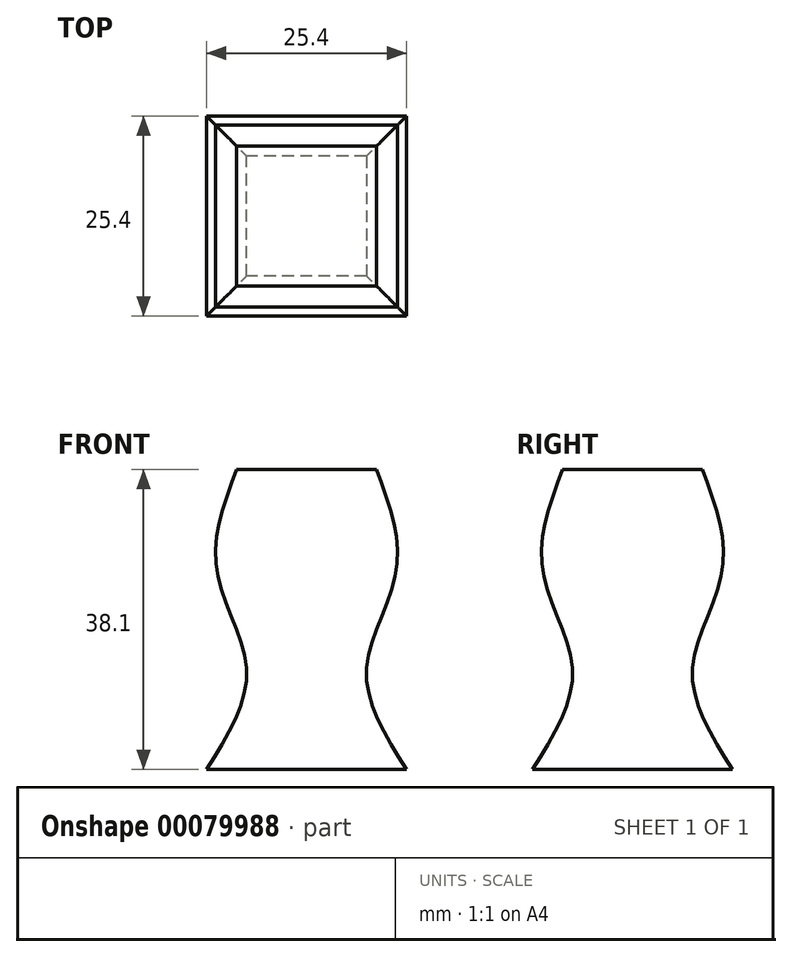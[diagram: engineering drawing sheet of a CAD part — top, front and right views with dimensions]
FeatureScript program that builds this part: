
annotation { "Feature Type Name" : "Feature", "Feature Type Description" : "" }
export const myFeature = defineFeature(function(context is Context, id is Id, definition is map)
    precondition{}
    {
        {
            var Q0;
            Q0=qCreatedBy(makeId("Top.planeOp"),FACE);
            cPlane(context, id + "F0", {"entities" : qUnion([Q0]), "cplaneType" : CPlaneType.OFFSET, "offset" : 12.7 * mm, "width" : 152.4 * mm, "height" : 152.4 * mm});
        }
        {
            var Q0;
            Q0=qCreatedBy(id+"F0.planeOp",FACE);
            cPlane(context, id + "F1", {"entities" : qUnion([Q0]), "cplaneType" : CPlaneType.OFFSET, "offset" : 12.7 * mm, "width" : 152.4 * mm, "height" : 152.4 * mm});
        }
        {
            var Q0;
            Q0=qCreatedBy(id+"F1.planeOp",FACE);
            cPlane(context, id + "F2", {"entities" : qUnion([Q0]), "cplaneType" : CPlaneType.OFFSET, "offset" : 12.7 * mm, "width" : 152.4 * mm, "height" : 152.4 * mm});
        }
        {
            var Q0;
            Q0=qCreatedBy(makeId("Top.planeOp"),FACE);
            var sketch = newSketch(context, id + "F3", { "sketchPlane" : qUnion([Q0])});
            skLineSegment(sketch, "E0.bottom", {"start": v(-12.7, 12.7) * mm, "end": v(12.7, 12.7) * mm});
            skLineSegment(sketch, "E0.top", {"start": v(-12.7, -12.7) * mm, "end": v(12.7, -12.7) * mm});
            skLineSegment(sketch, "E0.left", {"start": v(-12.7, 12.7) * mm, "end": v(-12.7, -12.7) * mm});
            skLineSegment(sketch, "E0.right", {"start": v(12.7, 12.7) * mm, "end": v(12.7, -12.7) * mm});
            skSolve(sketch);
        }
        {
            var Q0;
            Q0=qCreatedBy(id+"F0.planeOp",FACE);
            var sketch = newSketch(context, id + "F4", { "sketchPlane" : qUnion([Q0])});
            skLineSegment(sketch, "E1.bottom", {"start": v(-7.62, 7.62) * mm, "end": v(7.62, 7.62) * mm});
            skLineSegment(sketch, "E1.top", {"start": v(-7.62, -7.62) * mm, "end": v(7.62, -7.62) * mm});
            skLineSegment(sketch, "E1.left", {"start": v(-7.62, 7.62) * mm, "end": v(-7.62, -7.62) * mm});
            skLineSegment(sketch, "E1.right", {"start": v(7.62, 7.62) * mm, "end": v(7.62, -7.62) * mm});
            skSolve(sketch);
        }
        {
            var Q0;
            Q0=qCreatedBy(id+"F1.planeOp",FACE);
            var sketch = newSketch(context, id + "F5", { "sketchPlane" : qUnion([Q0])});
            skLineSegment(sketch, "E2.bottom", {"start": v(-11.43, 11.43) * mm, "end": v(11.43, 11.43) * mm});
            skLineSegment(sketch, "E2.top", {"start": v(-11.43, -11.43) * mm, "end": v(11.43, -11.43) * mm});
            skLineSegment(sketch, "E2.left", {"start": v(-11.43, 11.43) * mm, "end": v(-11.43, -11.43) * mm});
            skLineSegment(sketch, "E2.right", {"start": v(11.43, 11.43) * mm, "end": v(11.43, -11.43) * mm});
            skSolve(sketch);
        }
        {
            var Q0;
            Q0=qCreatedBy(id+"F2.planeOp",FACE);
            var sketch = newSketch(context, id + "F6", { "sketchPlane" : qUnion([Q0])});
            skLineSegment(sketch, "E3.bottom", {"start": v(-8.89, 8.89) * mm, "end": v(8.9, 8.9) * mm});
            skLineSegment(sketch, "E3.top", {"start": v(-8.89, -8.9) * mm, "end": v(8.9, -8.89) * mm});
            skLineSegment(sketch, "E3.left", {"start": v(-8.89, 8.89) * mm, "end": v(-8.89, -8.9) * mm});
            skLineSegment(sketch, "E3.right", {"start": v(8.9, 8.9) * mm, "end": v(8.9, -8.9) * mm});
            skSolve(sketch);
        }
        {
            var Q0;
            Q0=sQuery(id+"F3.wireOp",VERTEX,"E0.left.end");
            var Q1;
            Q1=sQuery(id+"F3.wireOp",VERTEX,"E0.top.end");
            var Q2;
            Q2=sQuery(id+"F4.wireOp",VERTEX,"E1.top.end");
            cPlane(context, id + "F7", {"entities" : qUnion([Q0, Q1, Q2]), "cplaneType" : CPlaneType.THREE_POINT, "offset" : 152.4 * mm, "width" : 152.4 * mm, "height" : 152.4 * mm});
        }
        {
            var Q0;
            Q0=qCreatedBy(id+"F7.planeOp",FACE);
            var sketch = newSketch(context, id + "F8", { "sketchPlane" : qUnion([Q0])});
            skLineSegment(sketch, "E4", {"start": v(12.7, -4.76) * mm, "end": v(-7.6, 8.98) * mm});
            skSolve(sketch);
        }
        {
            var Q0;
            Q0=sQuery(id+"F8.wireOp",VERTEX,"E4.end");
            var Q1;
            Q1=sQuery(id+"F4.wireOp",VERTEX,"E1.right.start");
            var Q2;
            Q2=sQuery(id+"F5.wireOp",VERTEX,"E2.right.start");
            cPlane(context, id + "F9", {"entities" : qUnion([Q0, Q1, Q2]), "cplaneType" : CPlaneType.THREE_POINT, "offset" : 152.4 * mm, "width" : 152.4 * mm, "height" : 152.4 * mm});
        }
        {
            var Q0;
            Q0=qCreatedBy(id+"F9.planeOp",FACE);
            var sketch = newSketch(context, id + "F10", { "sketchPlane" : qUnion([Q0])});
            skLineSegment(sketch, "E5", {"start": v(7.61, 14.29) * mm, "end": v(-11.46, 27.65) * mm});
            skSolve(sketch);
        }
        {
            var Q0;
            Q0=sQuery(id+"F10.wireOp",VERTEX,"E5.end");
            var Q1;
            Q1=sQuery(id+"F5.wireOp",VERTEX,"E2.left.start");
            var Q2;
            Q2=sQuery(id+"F6.wireOp",VERTEX,"E3.bottom.start");
            cPlane(context, id + "F11", {"entities" : qUnion([Q0, Q1, Q2]), "cplaneType" : CPlaneType.THREE_POINT, "offset" : 152.4 * mm, "width" : 152.4 * mm, "height" : 152.4 * mm});
        }
        {
            var Q0;
            Q0=qCreatedBy(id+"F11.planeOp",FACE);
            var sketch = newSketch(context, id + "F12", { "sketchPlane" : qUnion([Q0])});
            skLineSegment(sketch, "E6", {"start": v(11.4, 22.58) * mm, "end": v(-8.8, 35.6) * mm});
            skSolve(sketch);
        }
        {
            var Q0;
            Q0 = qSketchRegion(id + "F3", true);
            var Q1;
            Q1 = qSketchRegion(id + "F4", true);
            var Q2;
            Q2 = qSketchRegion(id + "F5", true);
            var Q3;
            Q3 = qSketchRegion(id + "F6", true);
            var Q4;
            Q4=sQuery(id+"F8.wireOp",EDGE,"E4");
            var Q5;
            Q5=sQuery(id+"F10.wireOp",EDGE,"E5");
            var Q6;
            Q6=sQuery(id+"F12.wireOp",EDGE,"E6");
            var Q7;
            Q7=sQuery(id+"F8.wireOp",VERTEX,"E4.start");
            var Q8;
            Q8=sQuery(id+"F8.wireOp",VERTEX,"E4.end");
            var Q9;
            Q9=sQuery(id+"F10.wireOp",VERTEX,"E5.end");
            var Q10;
            Q10=sQuery(id+"F12.wireOp",VERTEX,"E6.end");
            loft(context, id + "F13", {"sheetProfilesArray" : [{ "sheetProfileEntities" : qUnion([Q0]) }, { "sheetProfileEntities" : qUnion([Q1]) }, { "sheetProfileEntities" : qUnion([Q2]) }, { "sheetProfileEntities" : qUnion([Q3]) }], "guidesArray" : [{ "guideEntities" : qUnion([Q4]), "guideDerivativeType" : LoftGuideDerivativeType.DEFAULT, "guideDerivativeMagnitude" : 1 }, { "guideEntities" : qUnion([Q5]), "guideDerivativeType" : LoftGuideDerivativeType.DEFAULT, "guideDerivativeMagnitude" : 1 }, { "guideEntities" : qUnion([Q6]), "guideDerivativeType" : LoftGuideDerivativeType.DEFAULT, "guideDerivativeMagnitude" : 1 }], "connections" : [{ "connectionEntities" : qUnion([Q7, Q8, Q9, Q10]), "connectionEdgeQueries" : qUnion([]), "connectionEdgeParameters" : [] }]});
        }
    });
